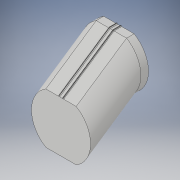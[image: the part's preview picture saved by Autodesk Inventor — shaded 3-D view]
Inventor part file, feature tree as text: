
AUTODESK INVENTOR PART (.ipt)
format: ipt  version: 2017 (Build 210142000, 142)  size: 153,088 bytes
history: native  units: in
note: dims shown in document units (in); Inventor stores cm internally (conversion verified against a paired STEP export)
features: sketch x2, extrude x1, plane x1, sweep x1
ambient origin geometry x8: Origin, YZ Plane, XZ Plane, XY Plane, X Axis, Y Axis, Z Axis, Center Point
bodies: Solid1 (feature_tree)
feature tree (5):
  sketch  "Sketch1"  dims[d0=6.6667in d3=1.0in d4=0.0in d12=8.0in]
  extrude  "connecction top"  Depth=6.6667in
  plane  "Work Plane2"
  sweep  "ramp"
  sketch  "Sketch6"  dims[d28=8.0in d45=0.0in d46=0.0in d65=0.8521in d66=4.0in d67=0.5833in d68=3.8873in d69=3.8873in d70=1.7083in d71=0.0625in d72=0.0625in d73=1.6458in d74=0.25in d75=0.125in d76=0.0892in d77=0.0884in d78=45.0deg d79=3.3333in d80=0.125in]
